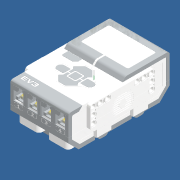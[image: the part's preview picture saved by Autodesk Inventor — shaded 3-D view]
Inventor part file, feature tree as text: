
AUTODESK INVENTOR PART (.ipt)
format: ipt  version: 2020 (Build 240168000, 168)  size: 5,711,872 bytes
history: native  units: mm
features: other x38, extrude x2, sketch x2, projected_geometry x1
ambient origin geometry x8: Origin, YZ Plane, XZ Plane, XY Plane, X Axis, Y Axis, Z Axis, Center Point
bodies: Solid1 (feature_tree), Solid2 (feature_tree), Solid3 (feature_tree), Solid4 (feature_tree), Solid5 (feature_tree), Solid6 (feature_tree), Solid7 (feature_tree), Solid8 (feature_tree), Solid9 (feature_tree), Solid10 (feature_tree), Solid11 (feature_tree), Solid12 (feature_tree), Solid13 (feature_tree), Solid14 (feature_tree), Solid15 (feature_tree), Solid16 (feature_tree), Solid17 (feature_tree), Solid18 (feature_tree), Solid19 (feature_tree), Solid20 (feature_tree), Solid21 (feature_tree), Solid22 (feature_tree), Solid23 (feature_tree), Solid24 (feature_tree), Solid25 (feature_tree), Solid26 (feature_tree), Solid27 (feature_tree), Solid28 (feature_tree), Solid29 (feature_tree), Solid30 (feature_tree), Solid31 (feature_tree), Solid32 (feature_tree), Solid33 (feature_tree), Solid34 (feature_tree), Solid35 (feature_tree), Solid36 (feature_tree), Solid37 (feature_tree), Solid38 (feature_tree)
feature tree (43):
  extrude  "Extrusion1"  Depth=61.5mm TaperAngle=0.0deg
  extrude  "Extrusion2"  [1 undecoded]
  sketch  "Sketch2"  dims[d0=21.0mm d1=0.0mm d2=61.5mm d3=0.0mm]
  sketch  "Sketch4"
  projected_geometry  "Projected Loop1"
  other  "99141p01-White_1:1"
  other  "11026-TransClear_1:1"
  other  "11030-LtBluishGray_1:1"
  other  "11036-LCD_1:1"
  other  "99145-LtBluishGray_1:1"
  other  "99145-LtBluishGray_2:1"
  other  "99146-LtBluishGray_1:1"
  other  "99147-LtBluishGray_1:1"
  other  "99147-LtBluishGray_2:1"
  other  "99148p01-TransClear_1:1"
  other  "99148p01-TransClear_1:2"
  other  "99141s01-LtBluishGray_1:1"
  other  "99141s01-LtBluishGray_1:2"
  other  "11142-LtBluishGray_1:1"
  other  "11143-LtBluishGray_1:1"
  other  "56554-ElectricAlloy_1:1"
  other  "56555-ElectricAlloy_1:1"
  other  "11177-TransGeen_1:1"
  other  "11177-TransRed_1:1"
  other  "11186-Black_1:1"
  other  "11186-Black_1:2"
  other  "u9208_1:1"
  other  "u9208_2:1"
  other  "u9208_3:1"
  other  "u9208_4:1"
  other  "u9208_5:1"
  other  "11025-White_1:1"
  other  "11025s02-LtBluishGray_1:1"
  other  "11025s02-LtBluishGray_1:2"
  other  "11032-Black_1:1"
  other  "11033-Black_1:1"
  other  "11034-Black_1:1"
  other  "11035-LtBluishGray_1:1"
  other  "54732b-LtBluishGray_1:1"
  other  "54732b-LtBluishGray_2:1"
  other  "54732b-LtBluishGray_3:1"
  other  "54732b-LtBluishGray_4:1"
  other  "97622-PCB_1:1"
note: 1 required parameter value undecoded (feature->parameter linkage not recoverable at this tier; creation-order binding heuristic only, values carry confidence <= 0.55)
